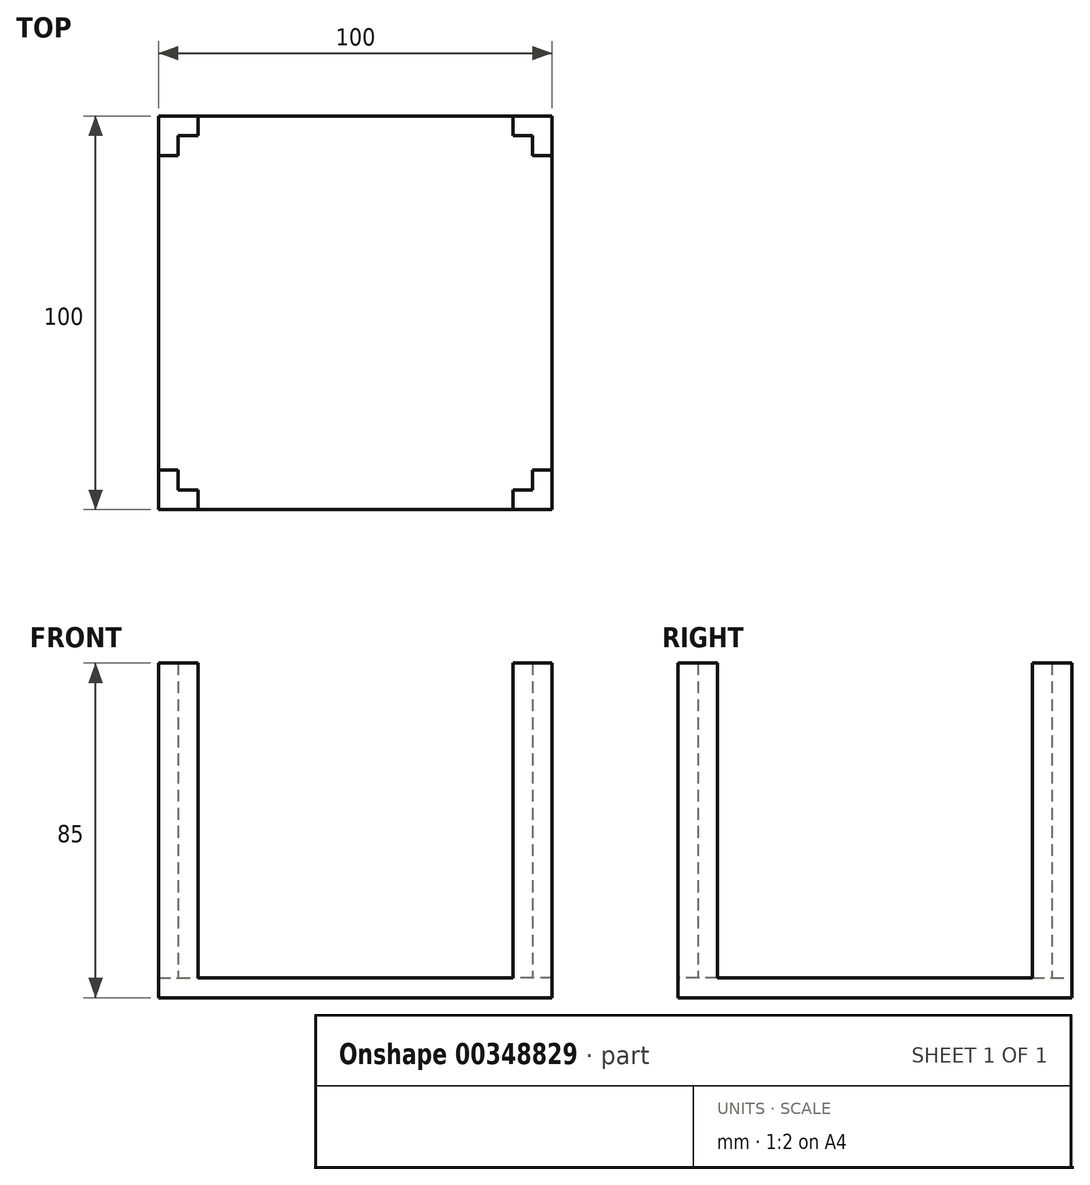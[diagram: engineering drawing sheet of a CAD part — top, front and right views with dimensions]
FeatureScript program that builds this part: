
annotation { "Feature Type Name" : "Feature", "Feature Type Description" : "" }
export const myFeature = defineFeature(function(context is Context, id is Id, definition is map)
    precondition{}
    {
        {
            var Q0;
            Q0=qCreatedBy(makeId("Top.planeOp"),FACE);
            var sketch = newSketch(context, id + "F0", { "sketchPlane" : qUnion([Q0])});
            skLineSegment(sketch, "E0", {"start": v(-50, 50) * mm, "end": v(-50, -50) * mm});
            skLineSegment(sketch, "E1", {"start": v(-50, -50) * mm, "end": v(50, -50) * mm});
            skLineSegment(sketch, "E2", {"start": v(50, -50) * mm, "end": v(50, 50) * mm});
            skLineSegment(sketch, "E3", {"start": v(-50, 50) * mm, "end": v(50, 50) * mm});
            skSolve(sketch);
        }
        {
            var Q0;
            Q0 = qSketchRegion(id + "F0", true);
            extrude(context, id + "F1", {"entities" : qUnion([Q0]), "depth" : 5 * mm});
        }
        {
            var Q0;
            Q0=makeQuery(id+"F1.opExtrude","CAP_FACE",FACE,{"disambiguationData":[OSD([sQuery(id+"F0.wireOp",EDGE,"atgMVXRX-dtva-iwla-UHJJ-75EoaK19bAIq"),sQuery(id+"F0.wireOp",EDGE,"E0"),sQuery(id+"F0.wireOp",EDGE,"E1"),sQuery(id+"F0.wireOp",EDGE,"E2"),sQuery(id+"F0.wireOp",EDGE,"inYuRvJJ-dPFk-IVl1-QbFG-775TjlZtBkgu")])],"isStart":false});
            var sketch = newSketch(context, id + "F2", { "sketchPlane" : qUnion([Q0])});
            skLineSegment(sketch, "E4", {"start": v(-40, 50) * mm, "end": v(-50, 50) * mm});
            skLineSegment(sketch, "E5", {"start": v(-50, 50) * mm, "end": v(-50, 40) * mm});
            skLineSegment(sketch, "E6", {"start": v(-50, 40) * mm, "end": v(-45, 40) * mm});
            skLineSegment(sketch, "E7", {"start": v(-45, 40) * mm, "end": v(-45, 45) * mm});
            skLineSegment(sketch, "E8", {"start": v(-45, 45) * mm, "end": v(-40, 45) * mm});
            skLineSegment(sketch, "E9", {"start": v(-40, 45) * mm, "end": v(-40, 50) * mm});
            skLineSegment(sketch, "E10.MirrorCS", {"start": v(45, 45) * mm, "end": v(40, 45) * mm});
            skLineSegment(sketch, "E11.MirrorCS", {"start": v(40, 45) * mm, "end": v(40, 50) * mm});
            skLineSegment(sketch, "E12.MirrorCS", {"start": v(45, 40) * mm, "end": v(45, 45) * mm});
            skLineSegment(sketch, "E13.MirrorCS", {"start": v(40, 50) * mm, "end": v(50, 50) * mm});
            skLineSegment(sketch, "E14.MirrorCS", {"start": v(50, 40) * mm, "end": v(45, 40) * mm});
            skLineSegment(sketch, "E15.MirrorCS", {"start": v(50, 50) * mm, "end": v(50, 40) * mm});
            skLineSegment(sketch, "E16.MirrorCS", {"start": v(-45, -45) * mm, "end": v(-40, -45) * mm});
            skLineSegment(sketch, "E17.MirrorCS", {"start": v(-45, -40) * mm, "end": v(-45, -45) * mm});
            skLineSegment(sketch, "E18.MirrorCS", {"start": v(45, -40) * mm, "end": v(45, -45) * mm});
            skLineSegment(sketch, "E19.MirrorCS", {"start": v(45, -45) * mm, "end": v(40, -45) * mm});
            skLineSegment(sketch, "E20.MirrorCS", {"start": v(-40, -45) * mm, "end": v(-40, -50) * mm});
            skLineSegment(sketch, "E21.MirrorCS", {"start": v(-50, -40) * mm, "end": v(-45, -40) * mm});
            skLineSegment(sketch, "E22.MirrorCS", {"start": v(-50, -50) * mm, "end": v(-50, -40) * mm});
            skLineSegment(sketch, "E23.MirrorCS", {"start": v(-40, -50) * mm, "end": v(-50, -50) * mm});
            skLineSegment(sketch, "E24.MirrorCS", {"start": v(40, -45) * mm, "end": v(40, -50) * mm});
            skLineSegment(sketch, "E25.MirrorCS", {"start": v(40, -50) * mm, "end": v(50, -50) * mm});
            skLineSegment(sketch, "E26.MirrorCS", {"start": v(50, -40) * mm, "end": v(45, -40) * mm});
            skLineSegment(sketch, "E27.MirrorCS", {"start": v(50, -50) * mm, "end": v(50, -40) * mm});
            skSolve(sketch);
        }
        {
            var Q0;
            Q0 = qSketchRegion(id + "F2", true);
            extrude(context, id + "F3", {"entities" : qUnion([Q0]), "operationType" : NewBodyOperationType.ADD, "depth" : 80 * mm});
        }
    });
